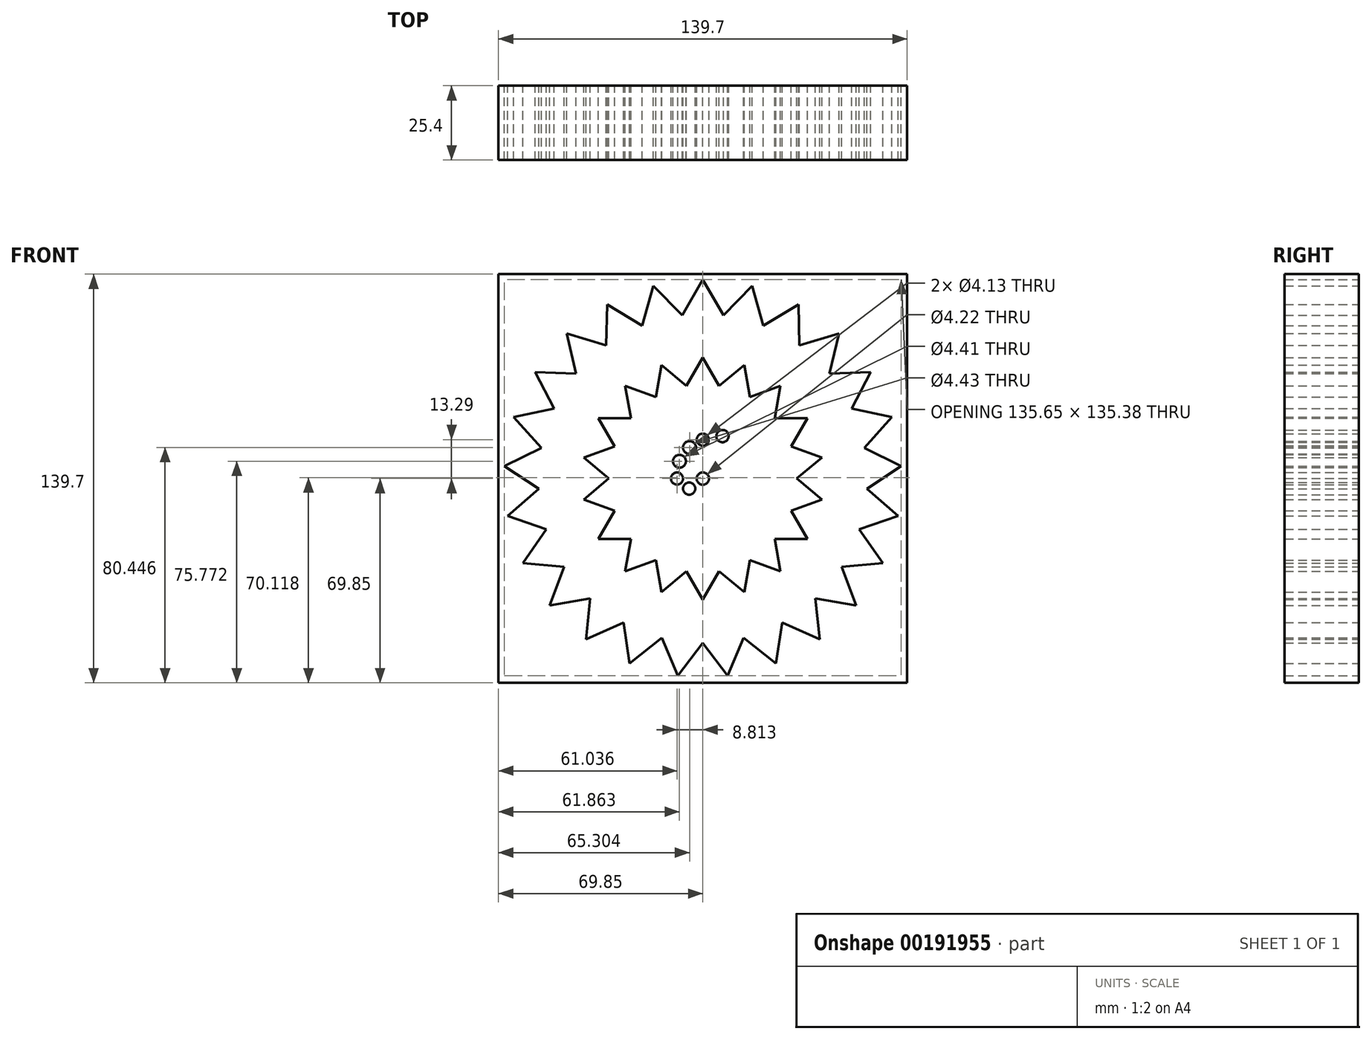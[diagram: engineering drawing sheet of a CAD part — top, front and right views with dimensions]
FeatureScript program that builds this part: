
annotation { "Feature Type Name" : "Feature", "Feature Type Description" : "" }
export const myFeature = defineFeature(function(context is Context, id is Id, definition is map)
    precondition{}
    {
        {
            var Q0;
            Q0=qCreatedBy(makeId("Front.planeOp"),FACE);
            var sketch = newSketch(context, id + "F0", { "sketchPlane" : qUnion([Q0])});
            skLineSegment(sketch, "E0.bottom", {"start": v(-69.85, 69.85) * mm, "end": v(69.85, 69.85) * mm});
            skLineSegment(sketch, "E0.top", {"start": v(-69.85, -69.85) * mm, "end": v(69.85, -69.85) * mm});
            skLineSegment(sketch, "E0.left", {"start": v(-69.85, 69.85) * mm, "end": v(-69.85, -69.85) * mm});
            skLineSegment(sketch, "E0.right", {"start": v(69.85, 69.85) * mm, "end": v(69.85, -69.85) * mm});
            skPoint(sketch, "E0.middle", {"position": v(0, 0) * mm});
            skSolve(sketch);
        }
        {
            var Q0;
            Q0=makeQuery(id+"F0.imprint","IMPRINT",FACE,{"disambiguationData":[TD([[makeQuery(id+"F0.imprint","IMPRINT",EDGE,{"derivedFrom":sQuery(id+"F0.wireOp",EDGE,"E0.bottom")}),-1.0]])]});
            extrude(context, id + "F1", {"entities" : qUnion([Q0]), "depth" : 25.4 * mm});
        }
        {
            var Q0;
            Q0=qCreatedBy(makeId("Front.planeOp"),FACE);
            var sketch = newSketch(context, id + "F2", { "sketchPlane" : qUnion([Q0])});
            skLineSegment(sketch, "E1", {"start": v(0, 67.96) * mm, "end": v(7.13, 55.61) * mm});
            skLineSegment(sketch, "E2", {"start": v(-7.13, 55.61) * mm, "end": v(0, 67.96) * mm});
            skLineSegment(sketch, "E3.1.0", {"start": v(-20.73, 52.1) * mm, "end": v(-16.9, 65.82) * mm});
            skLineSegment(sketch, "E3.1.1", {"start": v(-16.9, 65.82) * mm, "end": v(-6.93, 55.64) * mm});
            skLineSegment(sketch, "E3.2.0", {"start": v(-33.04, 45.3) * mm, "end": v(-32.74, 59.55) * mm});
            skLineSegment(sketch, "E3.2.1", {"start": v(-32.74, 59.55) * mm, "end": v(-20.55, 52.17) * mm});
            skLineSegment(sketch, "E3.3.0", {"start": v(-43.27, 35.66) * mm, "end": v(-46.52, 49.54) * mm});
            skLineSegment(sketch, "E3.3.1", {"start": v(-46.52, 49.54) * mm, "end": v(-32.88, 45.42) * mm});
            skLineSegment(sketch, "E3.4.0", {"start": v(-50.78, 23.78) * mm, "end": v(-57.38, 36.41) * mm});
            skLineSegment(sketch, "E3.4.1", {"start": v(-57.38, 36.41) * mm, "end": v(-43.14, 35.82) * mm});
            skLineSegment(sketch, "E3.5.0", {"start": v(-55.1, 10.4) * mm, "end": v(-64.63, 21) * mm});
            skLineSegment(sketch, "E3.5.1", {"start": v(-64.63, 21) * mm, "end": v(-50.7, 23.96) * mm});
            skLineSegment(sketch, "E3.6.0", {"start": v(-55.95, -3.62) * mm, "end": v(-67.82, 4.27) * mm});
            skLineSegment(sketch, "E3.6.1", {"start": v(-67.82, 4.27) * mm, "end": v(-55.06, 10.6) * mm});
            skLineSegment(sketch, "E3.7.0", {"start": v(-53.3, -17.42) * mm, "end": v(-66.75, -12.73) * mm});
            skLineSegment(sketch, "E3.7.1", {"start": v(-66.75, -12.73) * mm, "end": v(-55.96, -3.42) * mm});
            skLineSegment(sketch, "E3.8.0", {"start": v(-47.29, -30.13) * mm, "end": v(-61.5, -28.94) * mm});
            skLineSegment(sketch, "E3.8.1", {"start": v(-61.5, -28.94) * mm, "end": v(-53.36, -17.23) * mm});
            skLineSegment(sketch, "E3.9.0", {"start": v(-38.3, -40.94) * mm, "end": v(-52.36, -43.32) * mm});
            skLineSegment(sketch, "E3.9.1", {"start": v(-52.36, -43.32) * mm, "end": v(-47.4, -29.96) * mm});
            skLineSegment(sketch, "E3.10.0", {"start": v(-26.92, -49.18) * mm, "end": v(-39.95, -54.98) * mm});
            skLineSegment(sketch, "E3.10.1", {"start": v(-39.95, -54.98) * mm, "end": v(-38.46, -40.8) * mm});
            skLineSegment(sketch, "E3.11.0", {"start": v(-13.85, -54.33) * mm, "end": v(-25.02, -63.19) * mm});
            skLineSegment(sketch, "E3.11.1", {"start": v(-25.02, -63.19) * mm, "end": v(-27.1, -49.09) * mm});
            skLineSegment(sketch, "E3.12.0", {"start": v(0.1, -56.07) * mm, "end": v(-8.52, -67.42) * mm});
            skLineSegment(sketch, "E3.12.1", {"start": v(-8.52, -67.42) * mm, "end": v(-14.04, -54.28) * mm});
            skLineSegment(sketch, "E3.13.0", {"start": v(14.04, -54.28) * mm, "end": v(8.52, -67.42) * mm});
            skLineSegment(sketch, "E3.13.1", {"start": v(8.52, -67.42) * mm, "end": v(-0.1, -56.07) * mm});
            skLineSegment(sketch, "E3.14.0", {"start": v(27.1, -49.09) * mm, "end": v(25.02, -63.19) * mm});
            skLineSegment(sketch, "E3.14.1", {"start": v(25.02, -63.19) * mm, "end": v(13.85, -54.33) * mm});
            skLineSegment(sketch, "E3.15.0", {"start": v(38.46, -40.8) * mm, "end": v(39.95, -54.98) * mm});
            skLineSegment(sketch, "E3.15.1", {"start": v(39.95, -54.98) * mm, "end": v(26.92, -49.18) * mm});
            skLineSegment(sketch, "E3.16.0", {"start": v(47.4, -29.96) * mm, "end": v(52.36, -43.32) * mm});
            skLineSegment(sketch, "E3.16.1", {"start": v(52.36, -43.32) * mm, "end": v(38.3, -40.94) * mm});
            skLineSegment(sketch, "E3.17.0", {"start": v(53.36, -17.23) * mm, "end": v(61.5, -28.94) * mm});
            skLineSegment(sketch, "E3.17.1", {"start": v(61.5, -28.94) * mm, "end": v(47.29, -30.13) * mm});
            skPoint(sketch, "E3.center", {"position": v(0, 0) * mm});
            skLineSegment(sketch, "E4.1.18.0", {"start": v(55.96, -3.42) * mm, "end": v(66.75, -12.73) * mm});
            skLineSegment(sketch, "E4.3.18.0", {"start": v(66.75, -12.73) * mm, "end": v(53.3, -17.42) * mm});
            skLineSegment(sketch, "E4.1.19.0", {"start": v(55.06, 10.6) * mm, "end": v(67.82, 4.27) * mm});
            skLineSegment(sketch, "E4.3.19.0", {"start": v(67.82, 4.27) * mm, "end": v(55.95, -3.62) * mm});
            skLineSegment(sketch, "E5.1.20.0", {"start": v(50.7, 23.96) * mm, "end": v(64.63, 21) * mm});
            skLineSegment(sketch, "E5.3.20.0", {"start": v(64.63, 21) * mm, "end": v(55.1, 10.4) * mm});
            skLineSegment(sketch, "E5.1.21.0", {"start": v(43.14, 35.82) * mm, "end": v(57.38, 36.41) * mm});
            skLineSegment(sketch, "E5.3.21.0", {"start": v(57.38, 36.41) * mm, "end": v(50.78, 23.78) * mm});
            skLineSegment(sketch, "E6.1.22.0", {"start": v(32.88, 45.42) * mm, "end": v(46.52, 49.54) * mm});
            skLineSegment(sketch, "E6.3.22.0", {"start": v(46.52, 49.54) * mm, "end": v(43.27, 35.66) * mm});
            skLineSegment(sketch, "E6.1.23.0", {"start": v(20.55, 52.17) * mm, "end": v(32.74, 59.55) * mm});
            skLineSegment(sketch, "E6.3.23.0", {"start": v(32.74, 59.55) * mm, "end": v(33.04, 45.3) * mm});
            skLineSegment(sketch, "E6.1.24.0", {"start": v(6.93, 55.64) * mm, "end": v(16.9, 65.82) * mm});
            skLineSegment(sketch, "E6.3.24.0", {"start": v(16.9, 65.82) * mm, "end": v(20.73, 52.1) * mm});
            skSolve(sketch);
        }
        {
            var Q0;
            Q0 = qSketchRegion(id + "F2", true);
            extrude(context, id + "F3", {"entities" : qUnion([Q0]), "operationType" : NewBodyOperationType.REMOVE, "endBound" : BoundingType.THROUGH_ALL, "depth" : 25.4 * mm});
        }
        {
            var Q0;
            Q0=qCreatedBy(makeId("Front.planeOp"),FACE);
            var sketch = newSketch(context, id + "F4", { "sketchPlane" : qUnion([Q0])});
            skLineSegment(sketch, "E7", {"start": v(0, 41.3) * mm, "end": v(5.82, 31.21) * mm});
            skLineSegment(sketch, "E8", {"start": v(0, 41.3) * mm, "end": v(-5.82, 31.21) * mm});
            skPoint(sketch, "E9.orphan", {"position": v(12.7, 19.3) * mm});
            skPoint(sketch, "E10.orphan", {"position": v(-12.7, 19.3) * mm});
            skLineSegment(sketch, "E11.1.0", {"start": v(-14.12, 38.8) * mm, "end": v(-5.2, 31.32) * mm});
            skLineSegment(sketch, "E11.1.1", {"start": v(-14.12, 38.8) * mm, "end": v(-16.15, 27.34) * mm});
            skLineSegment(sketch, "E11.2.0", {"start": v(-26.55, 31.64) * mm, "end": v(-15.6, 27.65) * mm});
            skLineSegment(sketch, "E11.2.1", {"start": v(-26.55, 31.64) * mm, "end": v(-24.52, 20.17) * mm});
            skLineSegment(sketch, "E11.3.0", {"start": v(-35.77, 20.65) * mm, "end": v(-24.12, 20.65) * mm});
            skLineSegment(sketch, "E11.3.1", {"start": v(-35.77, 20.65) * mm, "end": v(-29.94, 10.56) * mm});
            skLineSegment(sketch, "E11.4.0", {"start": v(-40.67, 7.17) * mm, "end": v(-29.73, 11.16) * mm});
            skLineSegment(sketch, "E11.4.1", {"start": v(-40.67, 7.17) * mm, "end": v(-31.75, -0.32) * mm});
            skLineSegment(sketch, "E11.5.0", {"start": v(-40.67, -7.17) * mm, "end": v(-31.75, 0.32) * mm});
            skLineSegment(sketch, "E11.5.1", {"start": v(-40.67, -7.17) * mm, "end": v(-29.73, -11.16) * mm});
            skLineSegment(sketch, "E11.6.0", {"start": v(-35.77, -20.65) * mm, "end": v(-29.94, -10.56) * mm});
            skLineSegment(sketch, "E11.6.1", {"start": v(-35.77, -20.65) * mm, "end": v(-24.12, -20.65) * mm});
            skLineSegment(sketch, "E11.7.0", {"start": v(-26.55, -31.64) * mm, "end": v(-24.52, -20.17) * mm});
            skLineSegment(sketch, "E11.7.1", {"start": v(-26.55, -31.64) * mm, "end": v(-15.6, -27.65) * mm});
            skLineSegment(sketch, "E11.8.0", {"start": v(-14.12, -38.8) * mm, "end": v(-16.15, -27.34) * mm});
            skLineSegment(sketch, "E11.8.1", {"start": v(-14.12, -38.8) * mm, "end": v(-5.2, -31.32) * mm});
            skLineSegment(sketch, "E11.9.0", {"start": v(0, -41.3) * mm, "end": v(-5.82, -31.21) * mm});
            skLineSegment(sketch, "E11.9.1", {"start": v(0, -41.3) * mm, "end": v(5.82, -31.21) * mm});
            skLineSegment(sketch, "E11.10.0", {"start": v(14.12, -38.8) * mm, "end": v(5.2, -31.32) * mm});
            skLineSegment(sketch, "E11.10.1", {"start": v(14.12, -38.8) * mm, "end": v(16.15, -27.34) * mm});
            skLineSegment(sketch, "E11.11.0", {"start": v(26.55, -31.64) * mm, "end": v(15.6, -27.65) * mm});
            skLineSegment(sketch, "E11.11.1", {"start": v(26.55, -31.64) * mm, "end": v(24.52, -20.17) * mm});
            skLineSegment(sketch, "E11.12.0", {"start": v(35.77, -20.65) * mm, "end": v(24.12, -20.65) * mm});
            skLineSegment(sketch, "E11.12.1", {"start": v(35.77, -20.65) * mm, "end": v(29.94, -10.56) * mm});
            skLineSegment(sketch, "E11.13.0", {"start": v(40.67, -7.17) * mm, "end": v(29.73, -11.16) * mm});
            skLineSegment(sketch, "E11.13.1", {"start": v(40.67, -7.17) * mm, "end": v(31.75, 0.32) * mm});
            skLineSegment(sketch, "E11.14.0", {"start": v(40.67, 7.17) * mm, "end": v(31.75, -0.32) * mm});
            skLineSegment(sketch, "E11.14.1", {"start": v(40.67, 7.17) * mm, "end": v(29.73, 11.16) * mm});
            skLineSegment(sketch, "E11.15.0", {"start": v(35.77, 20.65) * mm, "end": v(29.94, 10.56) * mm});
            skLineSegment(sketch, "E11.15.1", {"start": v(35.77, 20.65) * mm, "end": v(24.12, 20.65) * mm});
            skLineSegment(sketch, "E11.16.0", {"start": v(26.55, 31.64) * mm, "end": v(24.52, 20.17) * mm});
            skLineSegment(sketch, "E11.16.1", {"start": v(26.55, 31.64) * mm, "end": v(15.6, 27.65) * mm});
            skLineSegment(sketch, "E11.17.0", {"start": v(14.12, 38.8) * mm, "end": v(16.15, 27.34) * mm});
            skLineSegment(sketch, "E11.17.1", {"start": v(14.12, 38.8) * mm, "end": v(5.2, 31.32) * mm});
            skPoint(sketch, "E11.center", {"position": v(0, 0) * mm});
            skSolve(sketch);
        }
        {
            var Q0;
            {var subQ12=sQuery(id+"F4.wireOp",EDGE,"E7");var subQ50=sQuery(id+"F4.wireOp",EDGE,"E8");var subQ54=makeQuery(id+"F4.imprint","INTERSECT",VERTEX,{"derivedFrom":[subQ12,subQ50]});Q0=makeQuery(id+"F4.imprint","IMPRINT",FACE,{"disambiguationData":[TD([[makeQuery(id+"F4.imprint","IMPRINT",EDGE,{"disambiguationData":[TD([[subQ54,-1.0]])],"derivedFrom":subQ12}),-1.0]])]});}
            extrude(context, id + "F5", {"entities" : qUnion([Q0]), "depth" : 25.4 * mm});
        }
        {
            var Q0;
            Q0=makeQuery(id+"F5.opExtrude","CAP_FACE",FACE,{"disambiguationData":[OSD([sQuery(id+"F4.wireOp",EDGE,"E7"),sQuery(id+"F4.wireOp",EDGE,"E8"),sQuery(id+"F4.wireOp",EDGE,"E11.1.0"),sQuery(id+"F4.wireOp",EDGE,"E11.1.1"),sQuery(id+"F4.wireOp",EDGE,"E11.2.0"),sQuery(id+"F4.wireOp",EDGE,"E11.2.1"),sQuery(id+"F4.wireOp",EDGE,"E11.3.0"),sQuery(id+"F4.wireOp",EDGE,"E11.3.1"),sQuery(id+"F4.wireOp",EDGE,"E11.4.0"),sQuery(id+"F4.wireOp",EDGE,"E11.4.1"),sQuery(id+"F4.wireOp",EDGE,"E11.5.0"),sQuery(id+"F4.wireOp",EDGE,"E11.5.1"),sQuery(id+"F4.wireOp",EDGE,"E11.6.0"),sQuery(id+"F4.wireOp",EDGE,"E11.6.1"),sQuery(id+"F4.wireOp",EDGE,"E11.7.0"),sQuery(id+"F4.wireOp",EDGE,"E11.7.1"),sQuery(id+"F4.wireOp",EDGE,"E11.8.0"),sQuery(id+"F4.wireOp",EDGE,"E11.8.1"),sQuery(id+"F4.wireOp",EDGE,"E11.9.0"),sQuery(id+"F4.wireOp",EDGE,"E11.9.1"),sQuery(id+"F4.wireOp",EDGE,"E11.10.0"),sQuery(id+"F4.wireOp",EDGE,"E11.10.1"),sQuery(id+"F4.wireOp",EDGE,"E11.11.0"),sQuery(id+"F4.wireOp",EDGE,"E11.11.1"),sQuery(id+"F4.wireOp",EDGE,"E11.12.0"),sQuery(id+"F4.wireOp",EDGE,"E11.12.1"),sQuery(id+"F4.wireOp",EDGE,"E11.13.0"),sQuery(id+"F4.wireOp",EDGE,"E11.13.1"),sQuery(id+"F4.wireOp",EDGE,"E11.14.0"),sQuery(id+"F4.wireOp",EDGE,"E11.14.1"),sQuery(id+"F4.wireOp",EDGE,"E11.15.0"),sQuery(id+"F4.wireOp",EDGE,"E11.15.1"),sQuery(id+"F4.wireOp",EDGE,"E11.16.0"),sQuery(id+"F4.wireOp",EDGE,"E11.16.1"),sQuery(id+"F4.wireOp",EDGE,"E11.17.0"),sQuery(id+"F4.wireOp",EDGE,"E11.17.1")])],"isStart":true});
            var sketch = newSketch(context, id + "F6", { "sketchPlane" : qUnion([Q0])});
            skCircle(sketch, "E12", {"center": v(0, 0) * mm, "radius": 2.11 * mm});
            skCircle(sketch, "E13", {"center": v(4.68, -3.44) * mm, "radius": 2.1 * mm});
            skCircle(sketch, "E14", {"center": v(8.81, 0) * mm, "radius": 2.07 * mm});
            skCircle(sketch, "E15", {"center": v(7.99, 5.92) * mm, "radius": 2.2 * mm});
            skCircle(sketch, "E16", {"center": v(4.55, 10.6) * mm, "radius": 2.22 * mm});
            skCircle(sketch, "E17", {"center": v(0, 13.29) * mm, "radius": 2.07 * mm});
            skCircle(sketch, "E18", {"center": v(-6.72, 14.51) * mm, "radius": 2.1 * mm});
            skSolve(sketch);
        }
        {
            var Q0;
            Q0 = qSketchRegion(id + "F6", true);
            extrude(context, id + "F7", {"entities" : qUnion([Q0]), "operationType" : NewBodyOperationType.REMOVE, "endBound" : BoundingType.THROUGH_ALL, "oppositeDirection" : true, "depth" : 25.4 * mm});
        }
    });
